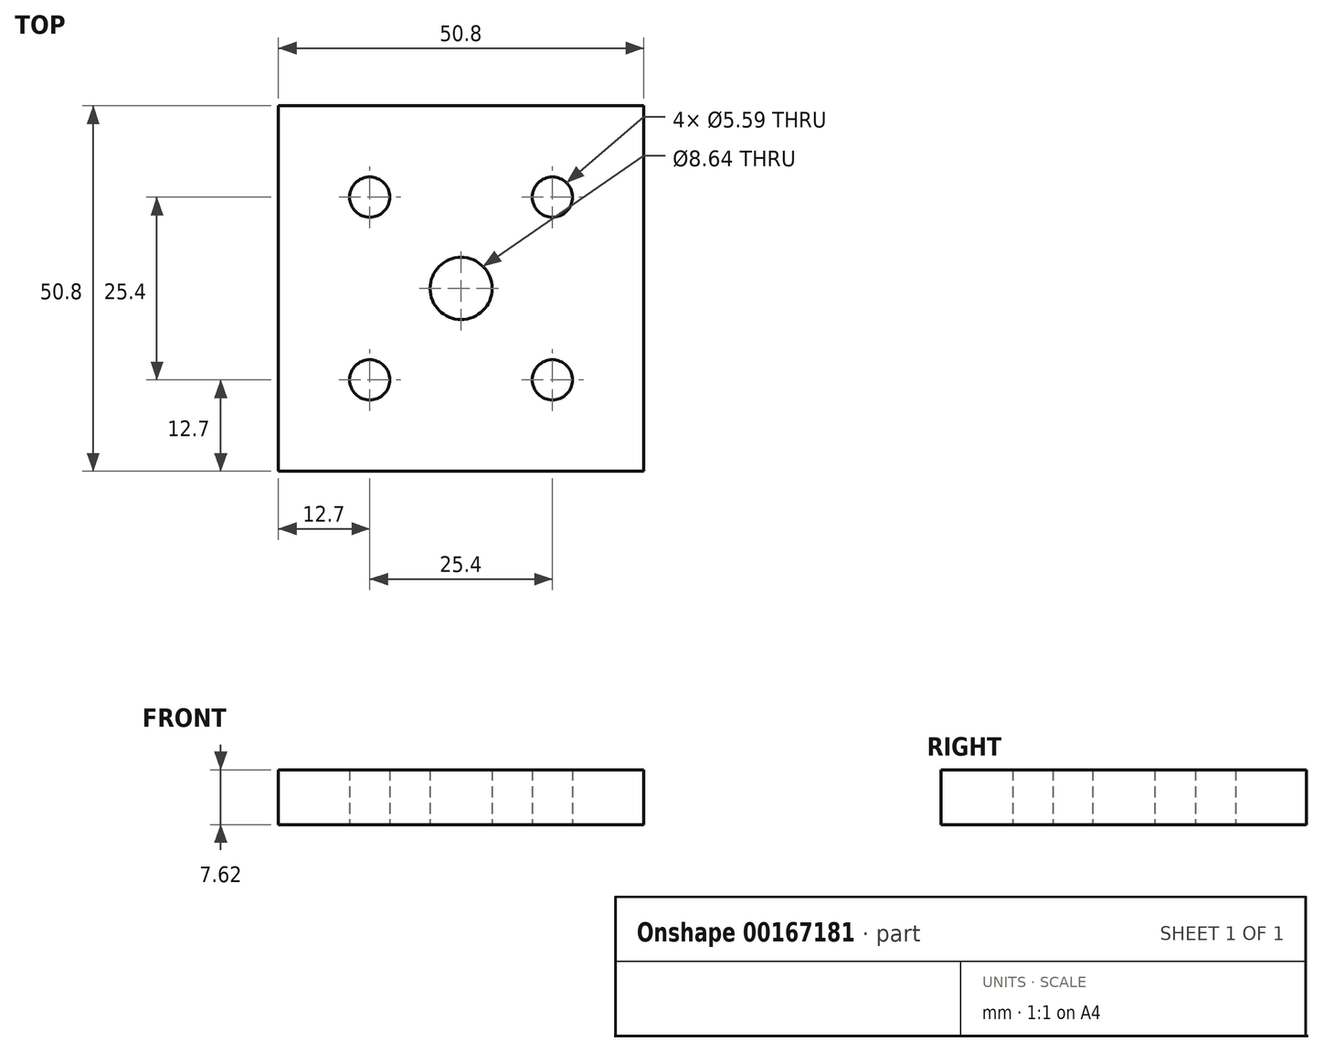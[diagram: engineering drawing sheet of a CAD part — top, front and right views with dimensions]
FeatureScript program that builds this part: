
annotation { "Feature Type Name" : "Feature", "Feature Type Description" : "" }
export const myFeature = defineFeature(function(context is Context, id is Id, definition is map)
    precondition{}
    {
        {
            var Q0;
            Q0=qCreatedBy(makeId("Top.planeOp"),FACE);
            var sketch = newSketch(context, id + "F0", { "sketchPlane" : qUnion([Q0])});
            skLineSegment(sketch, "E0.bottom", {"start": v(25.4, 25.4) * mm, "end": v(-25.4, 25.4) * mm});
            skLineSegment(sketch, "E0.top", {"start": v(25.4, -25.4) * mm, "end": v(-25.4, -25.4) * mm});
            skLineSegment(sketch, "E0.left", {"start": v(25.4, 25.4) * mm, "end": v(25.4, -25.4) * mm});
            skLineSegment(sketch, "E0.right", {"start": v(-25.4, 25.4) * mm, "end": v(-25.4, -25.4) * mm});
            skPoint(sketch, "E0.middle", {"position": v(0, 0) * mm});
            skLineSegment(sketch, "E1.bottom", {"start": v(12.7, 12.7) * mm, "end": v(-12.7, 12.7) * mm, "construction": true});
            skLineSegment(sketch, "E1.top", {"start": v(12.7, -12.7) * mm, "end": v(-12.7, -12.7) * mm, "construction": true});
            skLineSegment(sketch, "E1.left", {"start": v(12.7, 12.7) * mm, "end": v(12.7, -12.7) * mm, "construction": true});
            skLineSegment(sketch, "E1.right", {"start": v(-12.7, 12.7) * mm, "end": v(-12.7, -12.7) * mm, "construction": true});
            skCircle(sketch, "E2", {"center": v(-12.7, 12.7) * mm, "radius": 2.8 * mm});
            skCircle(sketch, "E3", {"center": v(12.7, 12.7) * mm, "radius": 2.8 * mm});
            skCircle(sketch, "E4", {"center": v(-12.7, -12.7) * mm, "radius": 2.8 * mm});
            skCircle(sketch, "E5", {"center": v(12.7, -12.7) * mm, "radius": 2.8 * mm});
            skCircle(sketch, "E6", {"center": v(0, 0) * mm, "radius": 4.32 * mm});
            skSolve(sketch);
        }
        {
            var Q0;
            Q0=makeQuery(id+"F0.imprint","IMPRINT",FACE,{"disambiguationData":[TD([[makeQuery(id+"F0.imprint","IMPRINT",EDGE,{"derivedFrom":sQuery(id+"F0.wireOp",EDGE,"E0.bottom")}),1.0]])]});
            extrude(context, id + "F1", {"entities" : qUnion([Q0]), "depth" : 7.62 * mm, "offsetDistance" : 30.48 * mm});
        }
    });
